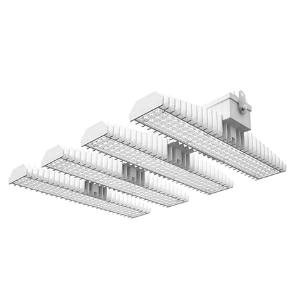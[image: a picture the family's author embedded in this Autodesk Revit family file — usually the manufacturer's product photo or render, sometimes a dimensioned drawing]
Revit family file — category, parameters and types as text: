
# Revit family: 3f_filippi_-_3f_lem_ho_ampio_3f_filippi_-_58974_a0811_-_3f_lem_4_ho_led_280_dali_cr_ampio___vt_a666
name_source: partatom
category: Lighting Fixtures
units: mm (PartAtom-declared; Revit-internal decimal feet)

## family parameters
Cut with Voids When Loaded = No
Host = Face
Light Source = No
Part Type = Normal
Room Calculation Point = No
Round Connector Dimension = Use Diameter
Shared = No

## types (1)
- 3F Filippi - 3F LEM HO Ampio (1 x LED, 42103 lm, 276 W, 4000 K)
    Apparent Load = 276 VA
    Approval mark = CE
    CIE Flux Codes = 60 92 99 100 100
    Color Rendering = 80
    Color Temperature = 4000 K
    Control Gear = Electronic transformer
    Default Elevation = 1800 mm
    Description = Industrial luminaire with high light output and high luminous efficiency designed with the most innovative technologies for environments with temperature up to 55°C.

ILLUMINOTECHNICAL
Luminous efficiency 100% (DLOR 99%, ULOR 1%).
Initial luminous flux of the luminaire 42103 lm.
Direct symmetric wide distribution: the illuminated area has a rectangular shape.
Installation Interdistance Transv.D = 1.58 x hu - Long.D = 1.45 x hu.
Tabular UGR (CIE 117 - 4H-8H; S=0.25H; 70/50/20): RUG 23.9 - 24.9.
Beam angle: 93° - 99°.
Luminous efficacy 153 lm/W.
Lifetime (L93/B10): 30000 h. (tq+25°C)
Lifetime (L90/B10): 50000 h. (tq+25°C)
Lifetime (L85/B10): 80000 h. (tq+25°C)
Lifetime (L80/B10): 100000 h. (tq+25°C)
Lifetime (L85/B10): 50000 h. (tq+55°C)
Sudden decreased luminous flux after 50000 hours: 0% (C0).
Photobiological safety in compliance with IEC/TR 62778: RG0 risk exempt, (IEC 62471).
In compliance with IEC/EN 62722-2-1 - IEC/EN 62717 standards.

SOURCE
4 Mid-Power linear LED modules 70W/840.
Energy efficiency class (UE 2019/2020 - UE 2019/2015): C.
CIE 13.3 Colour rendering index: CRI >80 (R9 <50%).
IES TM-30 Fidelity Index: Rf = 84 Rg = 95.
CCT nominal colour temperature 4000 K.
Colour initial tolerance (MacAdam): SDCM 3.

MECHANICAL
Passive modular heatsinks in die-casted aluminium, painted in white colour.
To optimize the thermal management of the LED module, the heatsinks are oversized and provided with self-cleaning of cooling fins.
Wiring body in aluminium and galvanised steel anchored solidly to the sinks and thermally separated.
3F Lens lenses with high luminous efficiency, transparent methacrylate (PMMA), fixed to the LED modules.
Fixing brackets in stainless steel.
Luminaire with limited surface temperature. - D - (EN 60598-2-24)
Dimensions: 757x542 mm, height 133 mm. Weight 19.278 kg.
IP65 protection degree.
Mechanical strength to impacts IK06 (1 joule).
Glow-wire test resistance 650°C.

ELECTRICAL
Halogen Free DALI-2 DATI (Parts 251, 252, 253), PUSH-DIM, electronic wiring 230V-50/60Hz, power factor 0.97 at full load, THD <25%, constant output current, class I, 2 driver, 2 DALI addresses.
Power of the luminaire 276 W.
ENEC - CE.
SAFE FLICKER: PstLM=<1 and SVM=<0.4 (IEC TR 61547-1 and IEC TR 63158), to ensure a more comfortable and safe light.
Luminaire compliant with EN 60598-2-22 for power supply from a centralised emergency system CPSS (Central Power Supply System), not incorporated in the luminaire - high risk areas excluded. The default power and flux are 100% in AC and 15% in DC.
Ambient temperature from -30°C to +55°C.
Temperature class T6 max 85°C.
Quick connection via M25 5P connector with 9-13 mm tightening range.
Power unit positioned on a separate compartment by the LED module to ensure optimum temperatures of cabling components, to be inspectable and maintainable.
Relative humidity UR: <85%.

INSTALLATION
Ceiling / Suspended / Wall.
All accessories dedicated to this product are available on the Catalog and on our website www.3F-Filippi.com.

ACCESSORIES
A0811 - VT transparent glass, tempered, not flammable, with sealing gasket.
One required for each light module. The pack contains 10 pieces.

APPLICATIONS
In commercial environments, exhibition and industrial areas, stores, open areas.
Environments in which it is necessary a total protection against falling fragments (eg environments with foodstuffs or machines with moving parts or with extreme temperature changes), use luminaires with polycarbonate lenses.

LIGHT MANAGEMENT
Recommended minimum setting: 10%.
The luminaire, equipped with (DALI-2 DATI) driver, can be controlled manually with 3F Easy Dim technology or automatically/manually with wired or wireless DALI/D2D control systems.
The D2D driver guarantees interoperability with other devices with the same certification by making the following information available:
Device Data (Part 251), Energy Report (Part 252), Diagnosis & Maintenance (Part 253).
In electrical systems without a regulation system (manual or automatic) and DALI bus, a suitable jumper must be made on the DA-DA terminals of the appliance.

WARNING
Fixture not suitable for cold stores with an ambient temperature <0°C and/or relative humidity >85%.
Luminaire designed for disposal/recycling at end-of-life.
Replaceable (LED only) light source by a professional. Replaceable control gear by a professional.
    Height = 133 mm  [stored 0.436352 ft]
    Lamp = 1 x LED
    Lamp Light Flux = 42103 lm
    Lamp Power = 276 W
    Lamp count = 1
    Length = 757 mm
    Lifetime = 50000 h
    Luminous efficacy = 153 lm/W
    Manufacturer = 3F Filippi
    ModVariant = No
    Model = 3F Filippi - 58974+A0811 - 3F LEM 4 HO LED 280 DALI CR AMPIO + VT
    Mounting Place = Ceiling
    Mounting Type = Pendant
    Number of Poles = 1
    OnlyDefault = Yes
    Power Factor = 1
    Product Name = 3F Filippi - 3F LEM HO Ampio
    Product group = pendant luminaire
    ProductGroupID = 9
    Protection Class = Protection class I
    Protection Degree = IP 65
    RLX_Detail_Level = 1
    RLX_Emergency_Light_Flux = 0 lm
    RLX_Emergency_Type = 0
    RLX_Emergency_Type_DB = No
    RlxData = <blob elided: 120541 chars, md5=385a9f9a>
    Socket = socket
    Standby Power = 0 W
    System Light Flux = 42103 lm
    System Power = 276 W
    Type Comments = Product without accessories
    Type Image = 3f_filippi_-_lem_4__a0811.jpg
    URL = http://relux.com
    VarID = ---
    Voltage = 0 V
    Weight = 0.00 kg
    Width = 542 mm

note: [stored X ft] marks values corroborated as IEEE doubles in the binary element streams (Revit-internal decimal feet)

## geometry (parser evidence)
native form markers: Blend x4, Sweep x12
no freeform markers — native parametric forms only
